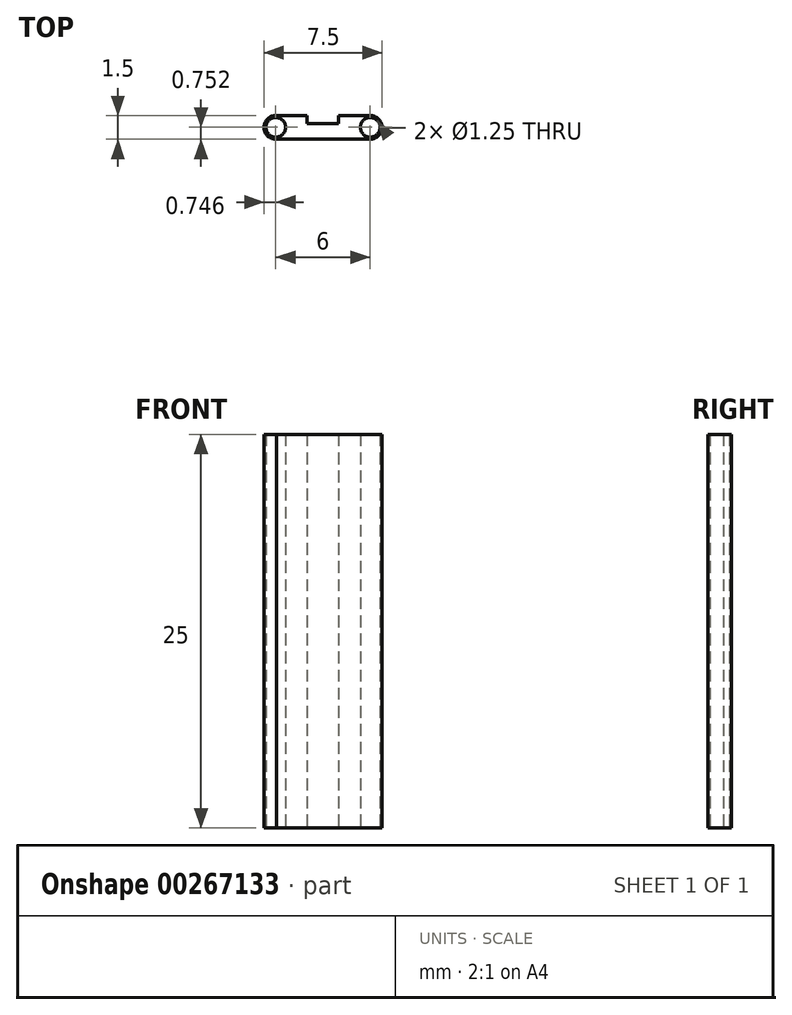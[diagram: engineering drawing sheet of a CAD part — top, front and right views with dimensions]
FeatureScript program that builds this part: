
annotation { "Feature Type Name" : "Feature", "Feature Type Description" : "" }
export const myFeature = defineFeature(function(context is Context, id is Id, definition is map)
    precondition{}
    {
        {
            var Q0;
            Q0=qCreatedBy(makeId("Top.planeOp"),FACE);
            var sketch = newSketch(context, id + "F0", { "sketchPlane" : qUnion([Q0])});
            skCircle(sketch, "E0", {"center": v(-78.2, 18.02) * mm, "radius": 0.62 * mm});
            skArc(sketch, "E1", {"start": v(-78.2, 17.27) * mm, "mid": v(-77.45, 18.02) * mm, "end": v(-78.2, 18.77) * mm});
            skCircle(sketch, "E2", {"center": v(-84.2, 18.02) * mm, "radius": 0.62 * mm});
            skArc(sketch, "E3", {"start": v(-84.19, 18.77) * mm, "mid": v(-84.95, 18.01) * mm, "end": v(-84.17, 17.27) * mm});
            skLineSegment(sketch, "E4", {"start": v(-84.24, 17.27) * mm, "end": v(-78.2, 17.27) * mm});
            skLineSegment(sketch, "E5", {"start": v(-84.22, 18.77) * mm, "end": v(-82.22, 18.77) * mm});
            skLineSegment(sketch, "E6", {"start": v(-82.22, 18.77) * mm, "end": v(-82.22, 18.27) * mm});
            skLineSegment(sketch, "E7", {"start": v(-82.22, 18.27) * mm, "end": v(-80.22, 18.27) * mm});
            skLineSegment(sketch, "E8", {"start": v(-80.22, 18.27) * mm, "end": v(-80.22, 18.77) * mm});
            skLineSegment(sketch, "E9.trimOffspring", {"start": v(-80.22, 18.77) * mm, "end": v(-78.2, 18.77) * mm});
            skSolve(sketch);
        }
        {
            var Q0;
            Q0 = qSketchRegion(id + "F0", true);
            extrude(context, id + "F1", {"entities" : qUnion([Q0]), "depth" : 25 * mm});
        }
    });
